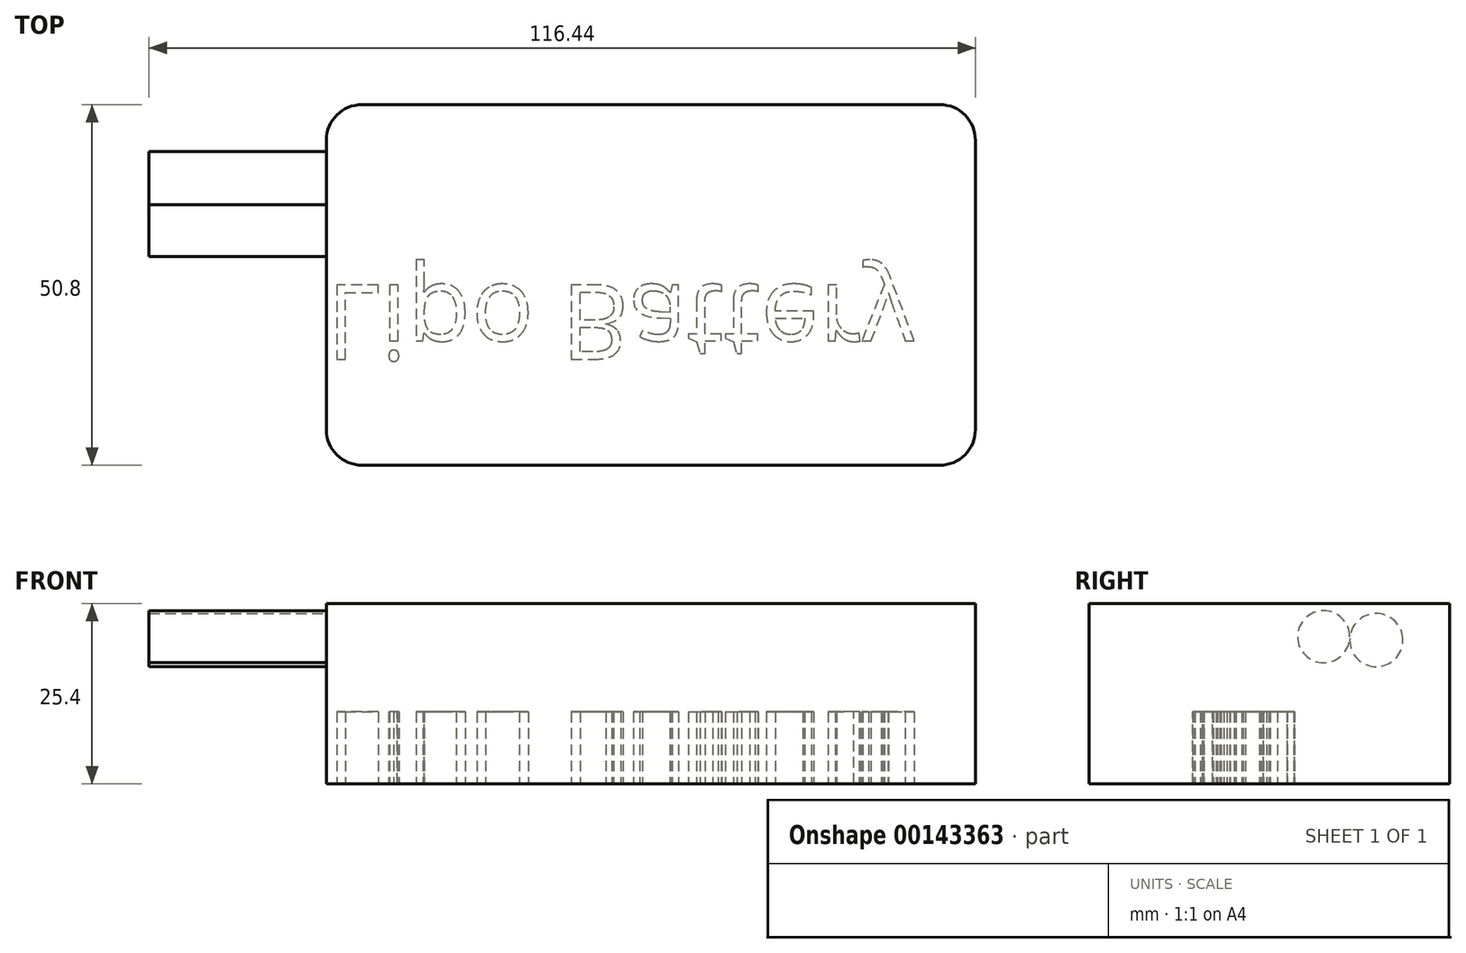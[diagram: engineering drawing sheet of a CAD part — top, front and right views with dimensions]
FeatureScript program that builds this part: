
annotation { "Feature Type Name" : "Feature", "Feature Type Description" : "" }
export const myFeature = defineFeature(function(context is Context, id is Id, definition is map)
    precondition{}
    {
        {
            var Q0;
            Q0=qCreatedBy(makeId("Top.planeOp"),FACE);
            var sketch = newSketch(context, id + "F0", { "sketchPlane" : qUnion([Q0])});
            skLineSegment(sketch, "E0.bottom", {"start": v(-45.72, 25.4) * mm, "end": v(45.72, 25.4) * mm});
            skLineSegment(sketch, "E0.top", {"start": v(-45.72, -25.4) * mm, "end": v(45.72, -25.4) * mm});
            skLineSegment(sketch, "E0.left", {"start": v(-45.72, 25.4) * mm, "end": v(-45.72, -25.4) * mm});
            skLineSegment(sketch, "E0.right", {"start": v(45.72, 25.4) * mm, "end": v(45.72, -25.4) * mm});
            skPoint(sketch, "E0.middle", {"position": v(0, 0) * mm});
            skSolve(sketch);
        }
        {
            var Q0;
            Q0=makeQuery(id+"F0.imprint","IMPRINT",FACE,{"disambiguationData":[TD([[makeQuery(id+"F0.imprint","IMPRINT",EDGE,{"derivedFrom":sQuery(id+"F0.wireOp",EDGE,"E0.bottom")}),-1.0]])]});
            extrude(context, id + "F1", {"entities" : qUnion([Q0]), "oppositeDirection" : true, "depth" : 25.4 * mm});
        }
        {
            var Q0;
            Q0=makeQuery(id+"F1.opExtrude","SWEPT_EDGE",EDGE,{"disambiguationData":[OSD([sQuery(id+"F0.wireOp",EDGE,"E0.top"),sQuery(id+"F0.wireOp",EDGE,"E0.right")])]});
            var Q1;
            Q1=makeQuery(id+"F1.opExtrude","SWEPT_EDGE",EDGE,{"disambiguationData":[OSD([sQuery(id+"F0.wireOp",EDGE,"E0.top"),sQuery(id+"F0.wireOp",EDGE,"E0.left")])]});
            var Q2;
            Q2=makeQuery(id+"F1.opExtrude","SWEPT_EDGE",EDGE,{"disambiguationData":[OSD([sQuery(id+"F0.wireOp",EDGE,"E0.bottom"),sQuery(id+"F0.wireOp",EDGE,"E0.right")])]});
            var Q3;
            Q3=makeQuery(id+"F1.opExtrude","SWEPT_EDGE",EDGE,{"disambiguationData":[OSD([sQuery(id+"F0.wireOp",EDGE,"E0.bottom"),sQuery(id+"F0.wireOp",EDGE,"E0.left")])]});
            fillet(context, id + "F2", {"entities" : qUnion([Q0, Q1, Q2, Q3]), "radius" : 5 * mm, "tangentPropagation" : true, "allowEdgeOverflow" : false});
        }
        {
            var Q0;
            Q0=makeQuery(id+"F1.opExtrude","CAP_FACE",FACE,{"disambiguationData":[OSD([sQuery(id+"F0.wireOp",EDGE,"E0.bottom"),sQuery(id+"F0.wireOp",EDGE,"E0.top"),sQuery(id+"F0.wireOp",EDGE,"E0.left"),sQuery(id+"F0.wireOp",EDGE,"E0.right")])],"isStart":true});
            var sketch = newSketch(context, id + "F3", { "sketchPlane" : qUnion([Q0])});
            skSolve(sketch);
        }
        {
            var Q0;
            Q0=makeQuery(id+"F1.opExtrude","SWEPT_FACE",FACE,{"disambiguationData":[OSD([sQuery(id+"F0.wireOp",EDGE,"E0.left")])]});
            var sketch = newSketch(context, id + "F4", { "sketchPlane" : qUnion([Q0])});
            skCircle(sketch, "E1", {"center": v(-15.08, -5.15) * mm, "radius": 3.75 * mm});
            skCircle(sketch, "E2", {"center": v(-7.66, -4.67) * mm, "radius": 3.66 * mm});
            skSolve(sketch);
        }
        {
            var Q0;
            Q0=makeQuery(id+"F4.imprint","IMPRINT",FACE,{"disambiguationData":[TD([[makeQuery(id+"F4.imprint","IMPRINT",EDGE,{"derivedFrom":sQuery(id+"F4.wireOp",EDGE,"E1")}),1.0]])]});
            extrude(context, id + "F5", {"entities" : qUnion([Q0]), "operationType" : NewBodyOperationType.ADD, "depth" : 25 * mm});
        }
        {
            var Q0;
            Q0 = qSketchRegion(id + "F4", true);
            var Q1;
            Q1=sQuery(id+"F4.wireOp",EDGE,"E2");
            extrude(context, id + "F6", {"entities" : qUnion([Q0]), "operationType" : NewBodyOperationType.ADD, "surfaceEntities" : qUnion([Q1]), "depth" : 25 * mm});
        }
        {
            var Q0;
            Q0=makeQuery(id+"F1.opExtrude","CAP_FACE",FACE,{"disambiguationData":[OSD([sQuery(id+"F0.wireOp",EDGE,"E0.bottom"),sQuery(id+"F0.wireOp",EDGE,"E0.top"),sQuery(id+"F0.wireOp",EDGE,"E0.left"),sQuery(id+"F0.wireOp",EDGE,"E0.right")])],"isStart":false});
            var sketch = newSketch(context, id + "F7", { "sketchPlane" : qUnion([Q0])});
            skText(sketch, "E3", { "text": "Lipo Battery", "fontName": "OpenSans-Regular.ttf"});
            const initialGuessF7  = {"E3": [-0.04572, -2e-05, 1, 0, 0.01059]};
            skSetInitialGuess(sketch, initialGuessF7);
            skSolve(sketch);
        }
        {
            var Q0;
            Q0 = qSketchRegion(id + "F7", true);
            extrude(context, id + "F8", {"entities" : qUnion([Q0]), "operationType" : NewBodyOperationType.REMOVE, "oppositeDirection" : true, "depth" : 10.16 * mm});
        }
    });
